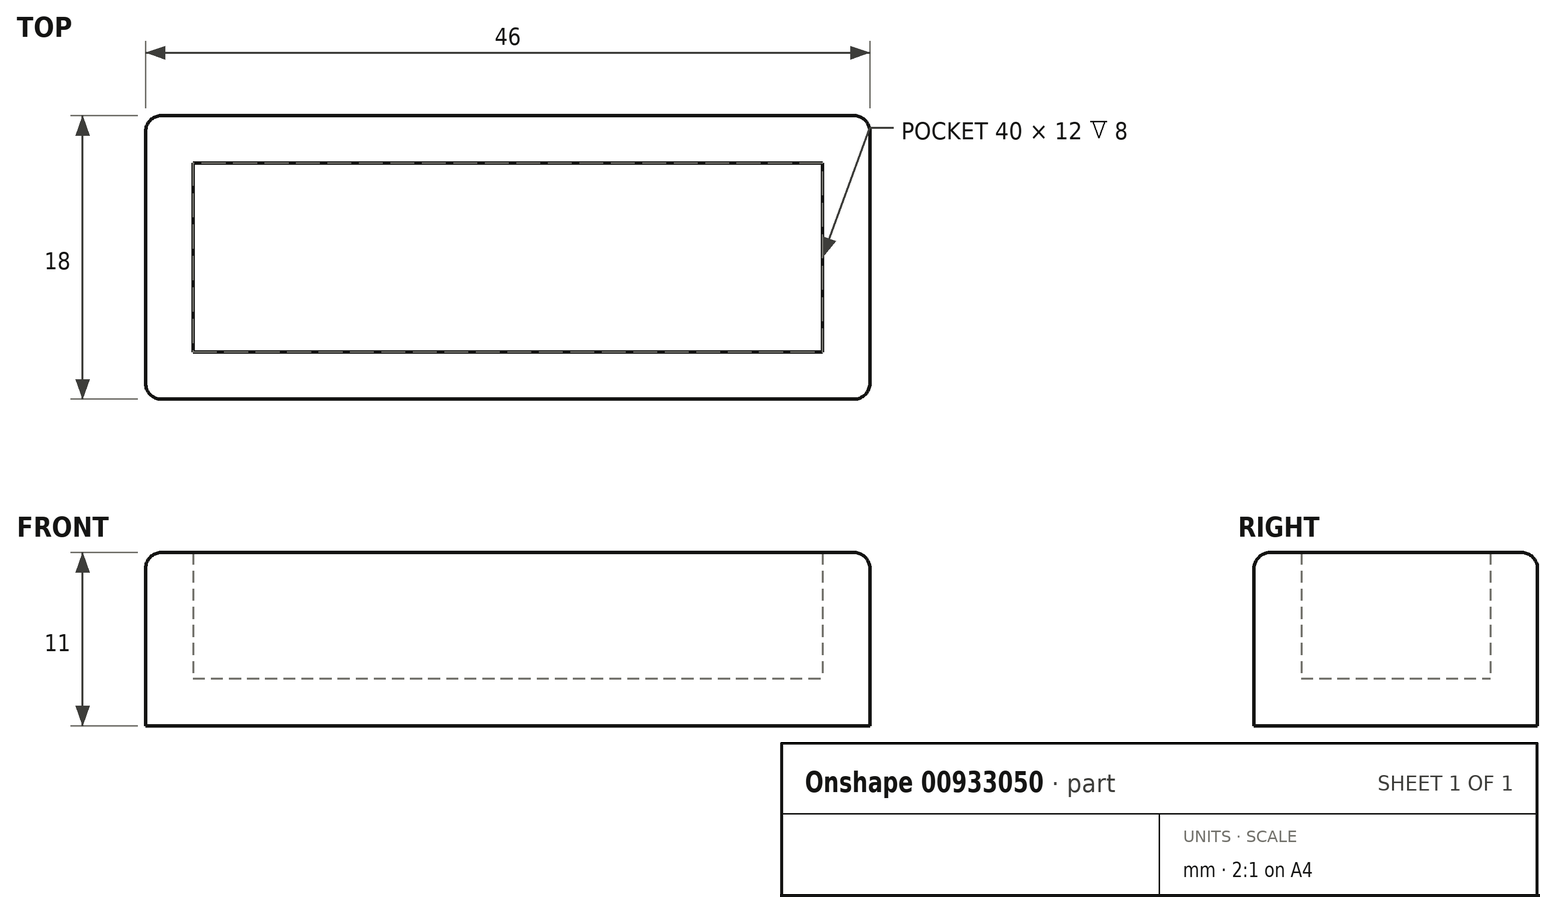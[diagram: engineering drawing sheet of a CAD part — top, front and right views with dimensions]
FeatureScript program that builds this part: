
annotation { "Feature Type Name" : "Feature", "Feature Type Description" : "" }
export const myFeature = defineFeature(function(context is Context, id is Id, definition is map)
    precondition{}
    {
        {
            var Q0;
            Q0=qCreatedBy(makeId("Top.planeOp"),FACE);
            var sketch = newSketch(context, id + "F0", { "sketchPlane" : qUnion([Q0])});
            skLineSegment(sketch, "E0.bottom", {"start": v(0, 0) * mm, "end": v(46, 0) * mm});
            skLineSegment(sketch, "E0.top", {"start": v(0, 18) * mm, "end": v(46, 18) * mm});
            skLineSegment(sketch, "E0.left", {"start": v(0, 0) * mm, "end": v(0, 18) * mm});
            skLineSegment(sketch, "E0.right", {"start": v(46, 0) * mm, "end": v(46, 18) * mm});
            skLineSegment(sketch, "E1.0", {"start": v(3, 15) * mm, "end": v(43, 15) * mm});
            skLineSegment(sketch, "E1.1", {"start": v(3, 3) * mm, "end": v(3, 15) * mm});
            skLineSegment(sketch, "E1.2", {"start": v(3, 3) * mm, "end": v(43, 3) * mm});
            skLineSegment(sketch, "E1.3", {"start": v(43, 3) * mm, "end": v(43, 15) * mm});
            skSolve(sketch);
        }
        {
            var Q0;
            Q0 = qSketchRegion(id + "F0", true);
            extrude(context, id + "F1", {"entities" : qUnion([Q0]), "depth" : 11 * mm, "offsetDistance" : 25 * mm});
        }
        {
            var Q0;
            Q0=qCreatedBy(makeId("Top.planeOp"),FACE);
            var sketch = newSketch(context, id + "F2", { "sketchPlane" : qUnion([Q0])});
            skLineSegment(sketch, "E2.0", {"start": v(3, 15) * mm, "end": v(43, 15) * mm});
            skLineSegment(sketch, "E3.0", {"start": v(3, 3) * mm, "end": v(3, 15) * mm});
            skLineSegment(sketch, "E4.0", {"start": v(3, 3) * mm, "end": v(43, 3) * mm});
            skLineSegment(sketch, "E5.0", {"start": v(43, 3) * mm, "end": v(43, 15) * mm});
            skSolve(sketch);
        }
        {
            var Q0;
            Q0 = qSketchRegion(id + "F2", true);
            extrude(context, id + "F3", {"entities" : qUnion([Q0]), "operationType" : NewBodyOperationType.ADD, "depth" : 3 * mm, "offsetDistance" : 25 * mm});
        }
        {
            var Q0;
            Q0=makeQuery(id+"F1.opExtrude","SWEPT_EDGE",EDGE,{"disambiguationData":[OSD([sQuery(id+"F0.wireOp",EDGE,"E0.top"),sQuery(id+"F0.wireOp",EDGE,"E0.right")])]});
            var Q1;
            Q1=makeQuery(id+"F1.opExtrude","SWEPT_EDGE",EDGE,{"disambiguationData":[OSD([sQuery(id+"F0.wireOp",EDGE,"E0.bottom"),sQuery(id+"F0.wireOp",EDGE,"E0.right")])]});
            var Q2;
            Q2=makeQuery(id+"F1.opExtrude","SWEPT_EDGE",EDGE,{"disambiguationData":[OSD([sQuery(id+"F0.wireOp",EDGE,"E0.bottom"),sQuery(id+"F0.wireOp",EDGE,"E0.left")])]});
            var Q3;
            Q3=makeQuery(id+"F1.opExtrude","SWEPT_EDGE",EDGE,{"disambiguationData":[OSD([sQuery(id+"F0.wireOp",EDGE,"E0.top"),sQuery(id+"F0.wireOp",EDGE,"E0.left")])]});
            var Q4;
            Q4=makeQuery(id+"F1.opExtrude","CAP_EDGE",EDGE,{"disambiguationData":[OSD([sQuery(id+"F0.wireOp",EDGE,"E0.top")])],"isStart":false});
            var Q5;
            Q5=makeQuery(id+"F1.opExtrude","CAP_EDGE",EDGE,{"disambiguationData":[OSD([sQuery(id+"F0.wireOp",EDGE,"E0.left")])],"isStart":false});
            var Q6;
            Q6=makeQuery(id+"F1.opExtrude","CAP_EDGE",EDGE,{"disambiguationData":[OSD([sQuery(id+"F0.wireOp",EDGE,"E0.bottom")])],"isStart":false});
            var Q7;
            Q7=makeQuery(id+"F1.opExtrude","CAP_EDGE",EDGE,{"disambiguationData":[OSD([sQuery(id+"F0.wireOp",EDGE,"E0.right")])],"isStart":false});
            fillet(context, id + "F4", {"entities" : qUnion([Q0, Q1, Q2, Q3, Q4, Q5, Q6, Q7]), "tangentPropagation" : true, "radius" : 1 * mm, "defaultsChanged" : false, "vertexSettings" : [], "allowEdgeOverflow" : false});
        }
    });
